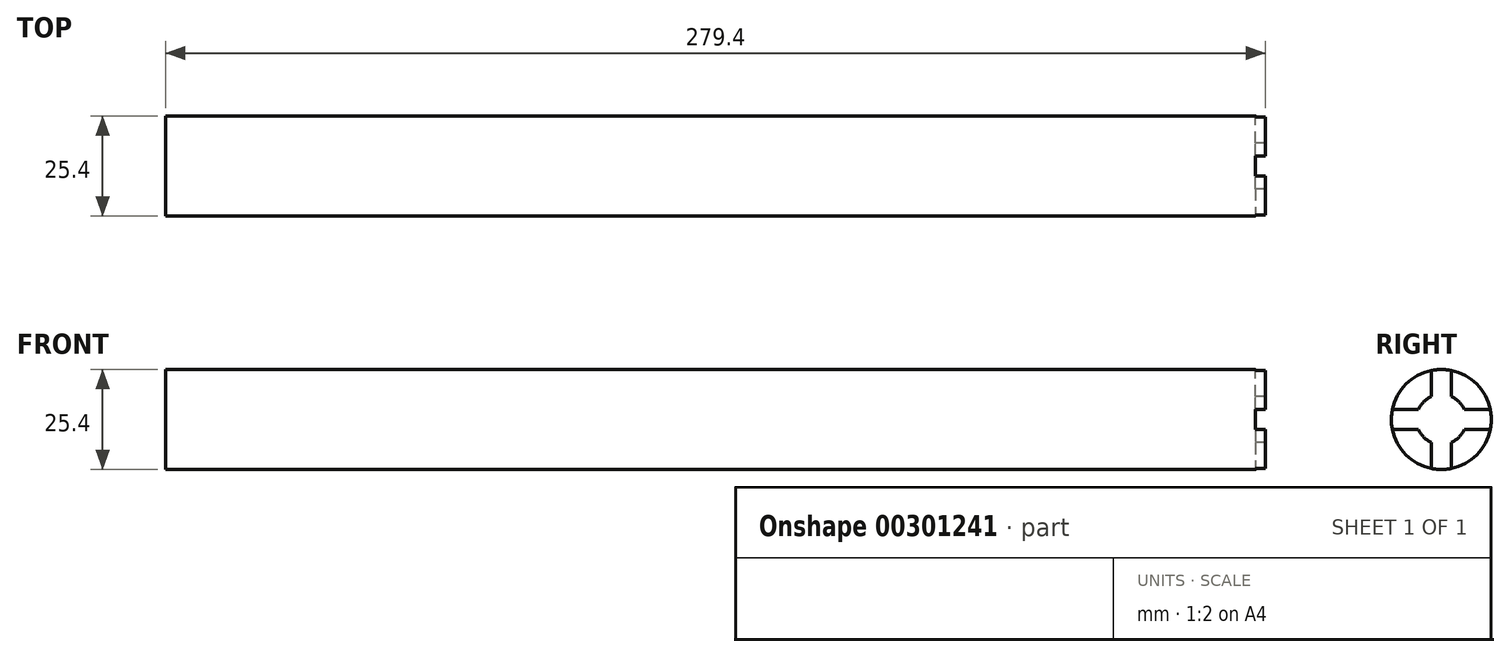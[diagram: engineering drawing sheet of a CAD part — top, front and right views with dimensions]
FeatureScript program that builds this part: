
annotation { "Feature Type Name" : "Feature", "Feature Type Description" : "" }
export const myFeature = defineFeature(function(context is Context, id is Id, definition is map)
    precondition{}
    {
        {
            var Q0;
            Q0=qCreatedBy(makeId("Right.planeOp"),FACE);
            var sketch = newSketch(context, id + "F0", { "sketchPlane" : qUnion([Q0])});
            skCircle(sketch, "E0", {"center": v(0, 0) * mm, "radius": 12.7 * mm});
            skSolve(sketch);
        }
        {
            var Q0;
            Q0 = qSketchRegion(id + "F0", true);
            extrude(context, id + "F1", {"entities" : qUnion([Q0]), "oppositeDirection" : true, "depth" : 276.86 * mm});
        }
        {
            var Q0;
            Q0=makeQuery(id+"F0.imprint","IMPRINT",FACE,{"disambiguationData":[TD([[makeQuery(id+"F0.imprint","IMPRINT",EDGE,{"derivedFrom":sQuery(id+"F0.wireOp",EDGE,"E0")}),1.0]])]});
            var sketch = newSketch(context, id + "F2", { "sketchPlane" : qUnion([Q0])});
            skCircle(sketch, "E1", {"center": v(0, 0) * mm, "radius": 6.35 * mm});
            skLineSegment(sketch, "E2", {"start": v(-2.54, 5.82) * mm, "end": v(-2.54, 12.44) * mm});
            skLineSegment(sketch, "E3", {"start": v(2.54, 5.82) * mm, "end": v(2.54, 12.44) * mm});
            skLineSegment(sketch, "E4", {"start": v(5.82, 2.54) * mm, "end": v(12.44, 2.54) * mm});
            skLineSegment(sketch, "E5", {"start": v(5.82, -2.54) * mm, "end": v(12.44, -2.54) * mm});
            skLineSegment(sketch, "E6", {"start": v(-2.54, -5.82) * mm, "end": v(-2.54, -12.44) * mm});
            skLineSegment(sketch, "E7", {"start": v(2.54, -5.82) * mm, "end": v(2.54, -12.44) * mm});
            skLineSegment(sketch, "E8", {"start": v(-5.82, 2.54) * mm, "end": v(-12.44, 2.54) * mm});
            skLineSegment(sketch, "E9", {"start": v(-5.82, -2.54) * mm, "end": v(-12.44, -2.54) * mm});
            skSolve(sketch);
        }
        {
            var Q0;
            {var subQ0=sQuery(id+"F2.wireOp",EDGE,"E2");Q0=makeQuery(id+"F2.imprint","IMPRINT",FACE,{"disambiguationData":[TD([[makeQuery(id+"F2.imprint","IMPRINT",EDGE,{"derivedFrom":subQ0}),1.0]])]});}
            var Q1;
            {var subQ0=sQuery(id+"F2.wireOp",EDGE,"E3");Q1=makeQuery(id+"F2.imprint","IMPRINT",FACE,{"disambiguationData":[TD([[makeQuery(id+"F2.imprint","IMPRINT",EDGE,{"derivedFrom":subQ0}),-1.0]])]});}
            var Q2;
            {var subQ0=sQuery(id+"F2.wireOp",EDGE,"E5");Q2=makeQuery(id+"F2.imprint","IMPRINT",FACE,{"disambiguationData":[TD([[makeQuery(id+"F2.imprint","IMPRINT",EDGE,{"derivedFrom":subQ0}),-1.0]])]});}
            var Q3;
            {var subQ0=sQuery(id+"F2.wireOp",EDGE,"E6");Q3=makeQuery(id+"F2.imprint","IMPRINT",FACE,{"disambiguationData":[TD([[makeQuery(id+"F2.imprint","IMPRINT",EDGE,{"derivedFrom":subQ0}),-1.0]])]});}
            extrude(context, id + "F3", {"entities" : qUnion([Q0, Q1, Q2, Q3]), "operationType" : NewBodyOperationType.ADD, "depth" : 2.54 * mm});
        }
    });
